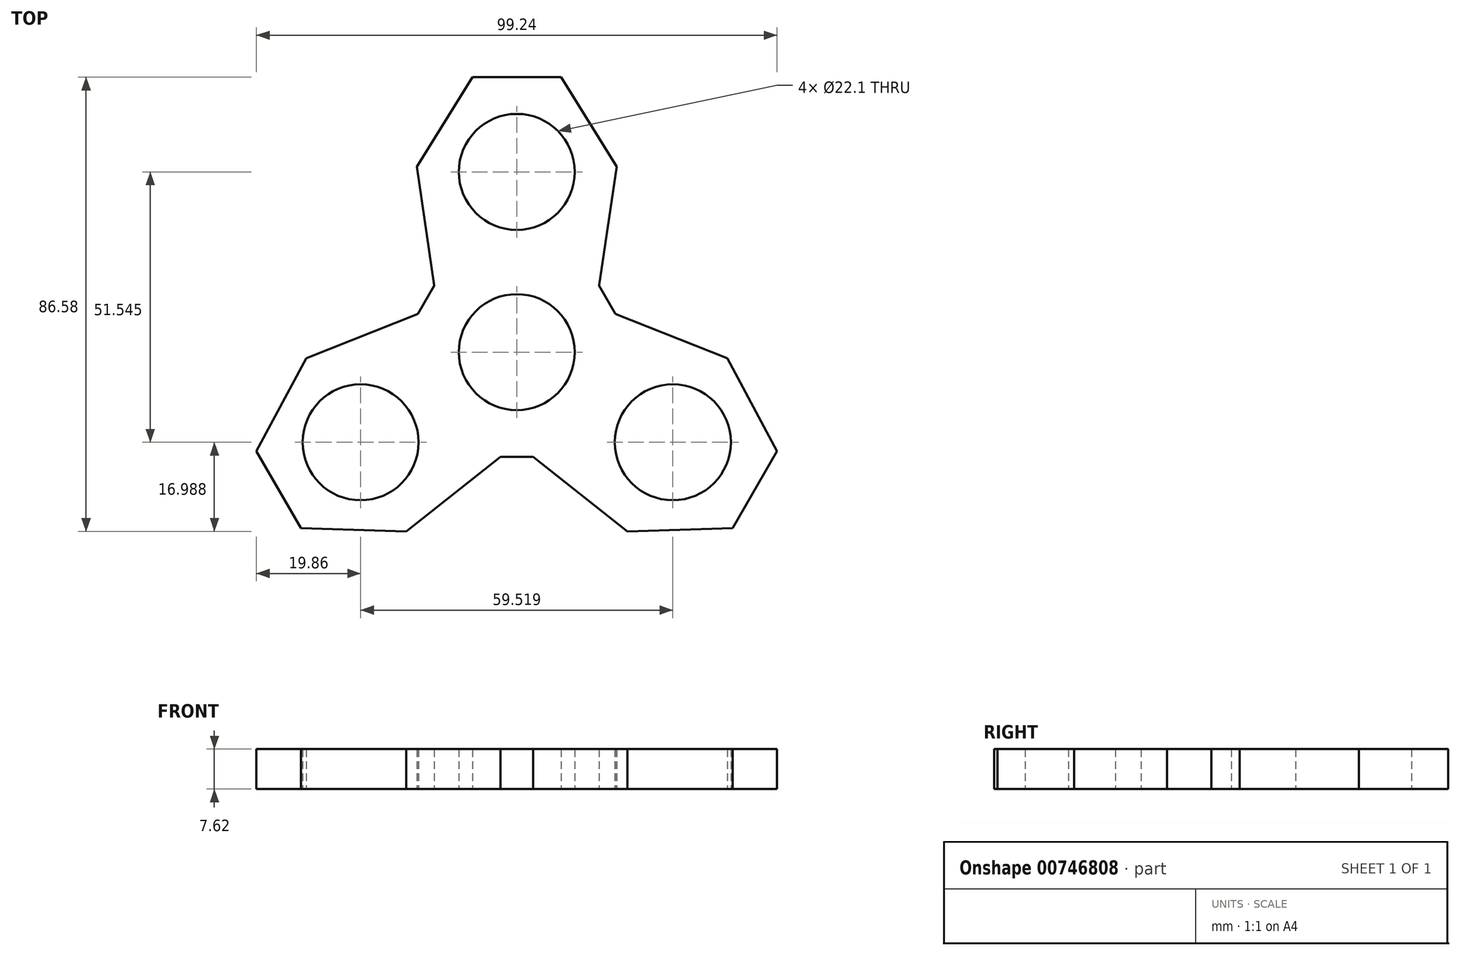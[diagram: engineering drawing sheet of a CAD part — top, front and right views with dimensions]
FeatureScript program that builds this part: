
annotation { "Feature Type Name" : "Feature", "Feature Type Description" : "" }
export const myFeature = defineFeature(function(context is Context, id is Id, definition is map)
    precondition{}
    {
        {
            var Q0;
            Q0=qCreatedBy(makeId("Top.planeOp"),FACE);
            var sketch = newSketch(context, id + "F0", { "sketchPlane" : qUnion([Q0])});
            skCircle(sketch, "E0", {"center": v(0, 0) * mm, "radius": 11.05 * mm});
            skCircle(sketch, "E1", {"center": v(0, 34.36) * mm, "radius": 11.05 * mm});
            skCircle(sketch, "E2.1.0", {"center": v(-29.76, -17.18) * mm, "radius": 11.05 * mm});
            skCircle(sketch, "E2.2.0", {"center": v(29.76, -17.18) * mm, "radius": 11.05 * mm});
            skLineSegment(sketch, "E3", {"start": v(-8.46, 52.41) * mm, "end": v(0, 52.41) * mm});
            skLineSegment(sketch, "E4", {"start": v(-8.46, 52.41) * mm, "end": v(-19.05, 35.36) * mm});
            skLineSegment(sketch, "E5.MirrorCS", {"start": v(8.46, 52.41) * mm, "end": v(0, 52.41) * mm});
            skLineSegment(sketch, "E6.MirrorCS", {"start": v(8.46, 52.41) * mm, "end": v(19.05, 35.36) * mm});
            skLineSegment(sketch, "E7", {"start": v(-19.05, 35.36) * mm, "end": v(-15.73, 12.67) * mm});
            skLineSegment(sketch, "E8.MirrorCS", {"start": v(19.05, 35.36) * mm, "end": v(15.73, 12.67) * mm});
            skLineSegment(sketch, "E9.1.0", {"start": v(-49.62, -18.88) * mm, "end": v(-45.39, -26.2) * mm});
            skLineSegment(sketch, "E9.1.1", {"start": v(-41.16, -33.53) * mm, "end": v(-45.39, -26.2) * mm});
            skLineSegment(sketch, "E9.1.2", {"start": v(-41.16, -33.53) * mm, "end": v(-21.1, -34.17) * mm});
            skLineSegment(sketch, "E9.1.3", {"start": v(-21.1, -34.17) * mm, "end": v(-3.11, -19.96) * mm});
            skLineSegment(sketch, "E9.1.4", {"start": v(-49.62, -18.88) * mm, "end": v(-40.14, -1.18) * mm});
            skLineSegment(sketch, "E9.1.5", {"start": v(-40.14, -1.18) * mm, "end": v(-18.84, 7.28) * mm});
            skLineSegment(sketch, "E9.2.0", {"start": v(41.16, -33.53) * mm, "end": v(45.39, -26.2) * mm});
            skLineSegment(sketch, "E9.2.1", {"start": v(49.62, -18.88) * mm, "end": v(45.39, -26.2) * mm});
            skLineSegment(sketch, "E9.2.2", {"start": v(49.62, -18.88) * mm, "end": v(40.14, -1.18) * mm});
            skLineSegment(sketch, "E9.2.3", {"start": v(40.14, -1.18) * mm, "end": v(18.84, 7.28) * mm});
            skLineSegment(sketch, "E9.2.4", {"start": v(41.16, -33.53) * mm, "end": v(21.1, -34.17) * mm});
            skLineSegment(sketch, "E9.2.5", {"start": v(21.1, -34.17) * mm, "end": v(3.11, -19.96) * mm});
            skLineSegment(sketch, "E10", {"start": v(-18.84, 7.28) * mm, "end": v(-15.73, 12.67) * mm});
            skLineSegment(sketch, "E11.1.0", {"start": v(3.11, -19.96) * mm, "end": v(-3.11, -19.96) * mm});
            skLineSegment(sketch, "E11.2.0", {"start": v(15.73, 12.67) * mm, "end": v(18.84, 7.28) * mm});
            skSolve(sketch);
        }
        {
            var Q0;
            Q0=makeQuery(id+"F0.imprint","IMPRINT",FACE,{"disambiguationData":[TD([[makeQuery(id+"F0.imprint","IMPRINT",EDGE,{"derivedFrom":sQuery(id+"F0.wireOp",EDGE,"E0")}),-1.0]])]});
            extrude(context, id + "F1", {"entities" : qUnion([Q0]), "depth" : 7.62 * mm, "offsetDistance" : 25.4 * mm});
        }
    });
